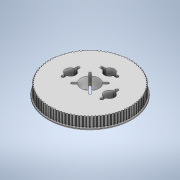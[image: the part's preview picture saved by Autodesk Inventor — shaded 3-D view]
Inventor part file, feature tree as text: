
AUTODESK INVENTOR PART (.ipt)
format: ipt  version: 2021 (Build 250183000, 183)  size: 1,652,736 bytes
history: native  units: mm
features: sketch x8, extrude x5, other x1, fillet x1
ambient origin geometry x8: Origin, YZ Plane, XZ Plane, XY Plane, X Axis, Y Axis, Z Axis, Center Point
bodies: Body1 (feature_tree)
feature tree (15):
  other  "Bryła1"
  extrude  "Wyciągnięcie proste1"  Depth=65.0mm
  sketch  "Szkic3"
  extrude  "Wyciągnięcie proste2"  Depth=1.5mm TaperAngle=0.0deg
  extrude  "Wyciągnięcie proste3"  Depth=420.0mm
  fillet  "Zaokrąglenie1"  Radius=420.0mm
  sketch  "Szkic17"
  sketch  "Szkic19"
  extrude  "Wyciągnięcie proste6"  Depth=7.5mm TaperAngle=0.0deg
  extrude  "Wyciągnięcie proste7"  TaperAngle=0.0deg  [1 undecoded]
  sketch  "Szkic25"
  sketch  "Szkic1"
  sketch  "Szkic15"
  sketch  "Szkic21"
  sketch  "Szkic24"
note: 1 required parameter value undecoded (feature->parameter linkage not recoverable at this tier; creation-order binding heuristic only, values carry confidence <= 0.55)
